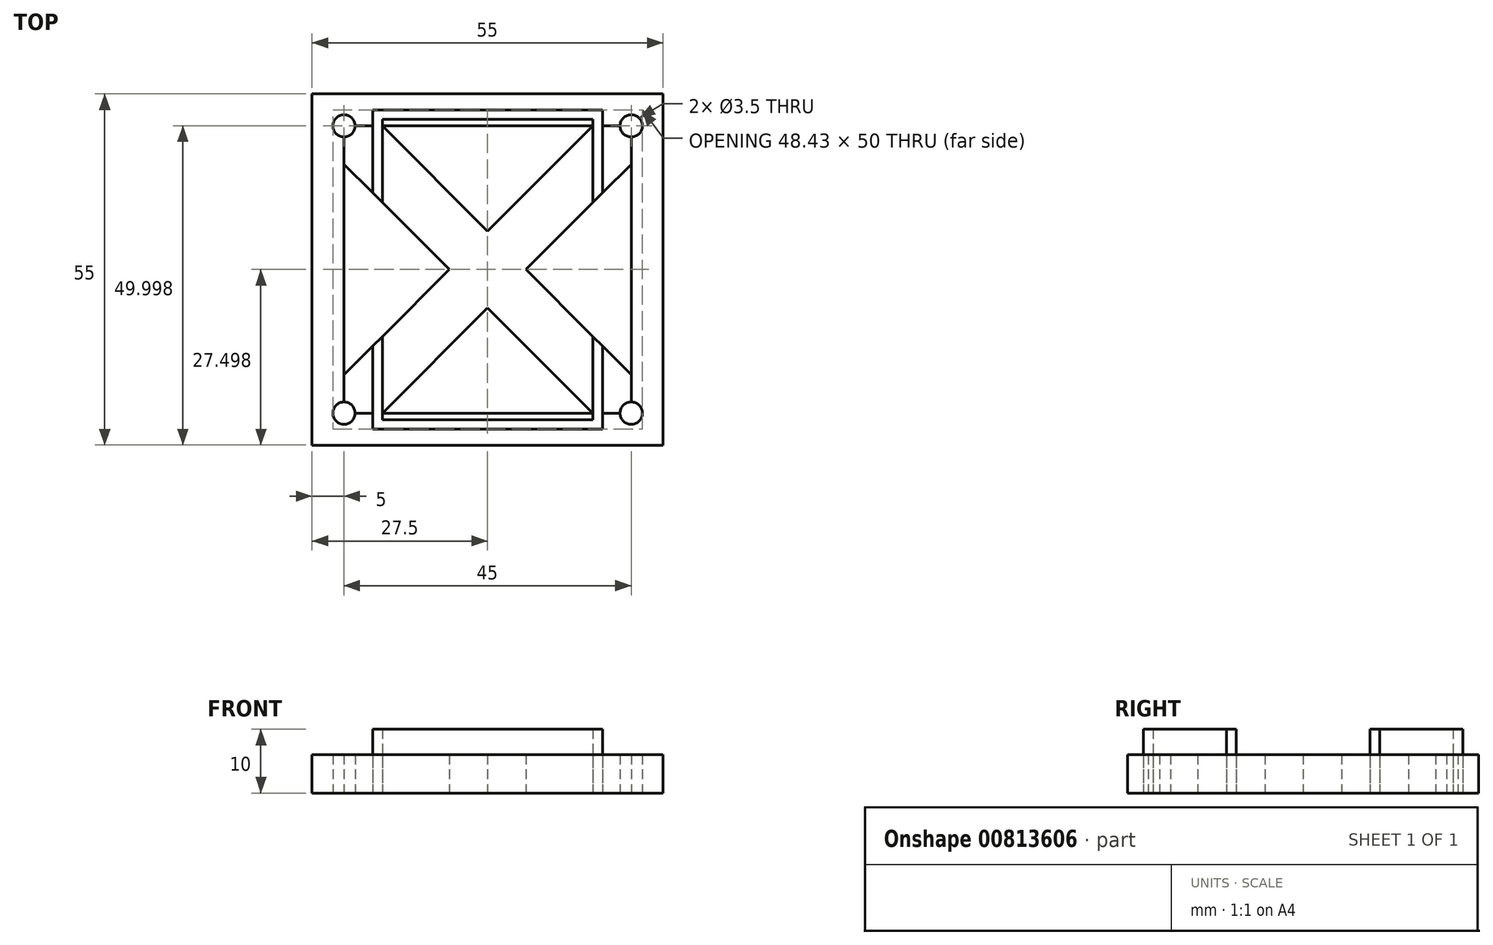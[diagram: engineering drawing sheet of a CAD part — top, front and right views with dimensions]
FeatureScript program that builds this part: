
annotation { "Feature Type Name" : "Feature", "Feature Type Description" : "" }
export const myFeature = defineFeature(function(context is Context, id is Id, definition is map)
    precondition{}
    {
        {
            var Q0;
            Q0=qCreatedBy(makeId("Top.planeOp"),FACE);
            var sketch = newSketch(context, id + "F0", { "sketchPlane" : qUnion([Q0])});
            skLineSegment(sketch, "E0.bottom", {"start": v(-44, 13.53) * mm, "end": v(11, 13.53) * mm});
            skLineSegment(sketch, "E0.top", {"start": v(-44, -41.47) * mm, "end": v(11, -41.47) * mm});
            skLineSegment(sketch, "E0.left", {"start": v(-44, 13.53) * mm, "end": v(-44, -41.47) * mm});
            skLineSegment(sketch, "E0.right", {"start": v(11, 13.53) * mm, "end": v(11, -41.47) * mm});
            skLineSegment(sketch, "E1.bottom", {"start": v(-39, 8.53) * mm, "end": v(6, 8.53) * mm});
            skLineSegment(sketch, "E1.top", {"start": v(-39, -36.47) * mm, "end": v(6, -36.47) * mm});
            skLineSegment(sketch, "E1.left", {"start": v(-39, 8.53) * mm, "end": v(-39, -36.47) * mm});
            skLineSegment(sketch, "E1.right", {"start": v(6, 8.53) * mm, "end": v(6, -36.47) * mm});
            skCircle(sketch, "E2", {"center": v(-39, 8.53) * mm, "radius": 1.75 * mm});
            skCircle(sketch, "E3", {"center": v(6, 8.53) * mm, "radius": 1.75 * mm});
            skCircle(sketch, "E4", {"center": v(6, -36.47) * mm, "radius": 1.75 * mm});
            skCircle(sketch, "E5", {"center": v(-39, -36.47) * mm, "radius": 1.75 * mm});
            skLineSegment(sketch, "E6.bottom", {"start": v(-33, 9.53) * mm, "end": v(0, 9.53) * mm});
            skLineSegment(sketch, "E6.top", {"start": v(-33, -37.47) * mm, "end": v(0, -37.47) * mm});
            skLineSegment(sketch, "E6.left", {"start": v(-33, 9.53) * mm, "end": v(-33, -37.47) * mm});
            skLineSegment(sketch, "E6.right", {"start": v(0, 9.53) * mm, "end": v(0, -37.47) * mm});
            skLineSegment(sketch, "E7.bottom", {"start": v(-34.5, 11.03) * mm, "end": v(1.5, 11.03) * mm});
            skLineSegment(sketch, "E7.top", {"start": v(-34.5, -38.97) * mm, "end": v(1.5, -38.97) * mm});
            skLineSegment(sketch, "E7.left", {"start": v(-34.5, 11.03) * mm, "end": v(-34.5, -38.97) * mm});
            skLineSegment(sketch, "E7.right", {"start": v(1.5, 11.03) * mm, "end": v(1.5, -38.97) * mm});
            skPoint(sketch, "E8", {"position": v(-16.38, -13.97) * mm});
            skPoint(sketch, "E9", {"position": v(-39, -30.47) * mm});
            skPoint(sketch, "E10", {"position": v(-33, -36.47) * mm});
            skPoint(sketch, "E11", {"position": v(0, -36.47) * mm});
            skPoint(sketch, "E12", {"position": v(6, -30.47) * mm});
            skPoint(sketch, "E13", {"position": v(6, 2.53) * mm});
            skPoint(sketch, "E14", {"position": v(0, 8.53) * mm});
            skPoint(sketch, "E15", {"position": v(-33, 8.53) * mm});
            skPoint(sketch, "E16", {"position": v(-39, 2.53) * mm});
            skLineSegment(sketch, "E17", {"start": v(-39, 2.53) * mm, "end": v(0, -36.47) * mm});
            skLineSegment(sketch, "E18", {"start": v(6, -30.47) * mm, "end": v(-33, 8.53) * mm});
            skLineSegment(sketch, "E19", {"start": v(0, 8.53) * mm, "end": v(-39, -30.47) * mm});
            skLineSegment(sketch, "E20", {"start": v(6, 2.53) * mm, "end": v(-33, -36.47) * mm});
            skSolve(sketch);
        }
        {
            var Q0;
            Q0=makeQuery(id+"F0.imprint","IMPRINT",FACE,{"disambiguationData":[TD([[makeQuery(id+"F0.imprint","IMPRINT",EDGE,{"derivedFrom":sQuery(id+"F0.wireOp",EDGE,"E0.bottom")}),-1.0]])]});
            var Q1;
            {var subQ0=sQuery(id+"F0.wireOp",EDGE,"E2");var subQ9=sQuery(id+"F0.wireOp",EDGE,"E1.bottom");var subQ10=makeQuery(id+"F0.imprint","INTERSECT",VERTEX,{"derivedFrom":[subQ9,subQ0]});Q1=makeQuery(id+"F0.imprint","IMPRINT",FACE,{"disambiguationData":[TD([[makeQuery(id+"F0.imprint","IMPRINT",EDGE,{"disambiguationData":[TD([[subQ10,-1.0]])],"derivedFrom":subQ9}),-1.0]])]});}
            var Q2;
            {var subQ5=sQuery(id+"F0.wireOp",EDGE,"E1.bottom");var subQ7=sQuery(id+"F0.wireOp",EDGE,"E7.right");var subQ11=makeQuery(id+"F0.imprint","INTERSECT",VERTEX,{"derivedFrom":[subQ5,subQ7]});Q2=makeQuery(id+"F0.imprint","IMPRINT",FACE,{"disambiguationData":[TD([[makeQuery(id+"F0.imprint","IMPRINT",EDGE,{"disambiguationData":[TD([[subQ11,-1.0]])],"derivedFrom":subQ5}),-1.0]])]});}
            var Q3;
            {var subQ5=sQuery(id+"F0.wireOp",EDGE,"E6.bottom");Q3=makeQuery(id+"F0.imprint","IMPRINT",FACE,{"disambiguationData":[TD([[makeQuery(id+"F0.imprint","IMPRINT",EDGE,{"derivedFrom":subQ5}),-1.0]])]});}
            var Q4;
            {var subQ5=sQuery(id+"F0.wireOp",EDGE,"E6.top");Q4=makeQuery(id+"F0.imprint","IMPRINT",FACE,{"disambiguationData":[TD([[makeQuery(id+"F0.imprint","IMPRINT",EDGE,{"derivedFrom":subQ5}),1.0]])]});}
            extrude(context, id + "F1", {"entities" : qUnion([Q0, Q1, Q2, Q3, Q4]), "depth" : 6 * mm, "offsetDistance" : 25 * mm});
        }
        {
            var Q0;
            {var subQ1=sQuery(id+"F0.wireOp",EDGE,"E6.bottom");Q0=makeQuery(id+"F0.imprint","IMPRINT",FACE,{"disambiguationData":[TD([[makeQuery(id+"F0.imprint","IMPRINT",EDGE,{"derivedFrom":subQ1}),1.0]])]});}
            var Q1;
            {var subQ0=sQuery(id+"F0.wireOp",EDGE,"E6.right");var subQ1=sQuery(id+"F0.wireOp",EDGE,"E1.bottom");var subQ2=makeQuery(id+"F0.imprint","INTERSECT",VERTEX,{"derivedFrom":[subQ1,subQ0]});Q1=makeQuery(id+"F0.imprint","IMPRINT",FACE,{"disambiguationData":[TD([[makeQuery(id+"F0.imprint","IMPRINT",EDGE,{"disambiguationData":[TD([[subQ2,-1.0]])],"derivedFrom":subQ1}),-1.0]])]});}
            var Q2;
            {var subQ0=sQuery(id+"F0.wireOp",EDGE,"E7.left");var subQ1=sQuery(id+"F0.wireOp",EDGE,"E1.bottom");var subQ2=makeQuery(id+"F0.imprint","INTERSECT",VERTEX,{"derivedFrom":[subQ1,subQ0]});Q2=makeQuery(id+"F0.imprint","IMPRINT",FACE,{"disambiguationData":[TD([[makeQuery(id+"F0.imprint","IMPRINT",EDGE,{"disambiguationData":[TD([[subQ2,-1.0]])],"derivedFrom":subQ1}),-1.0]])]});}
            var Q3;
            {var subQ1=sQuery(id+"F0.wireOp",EDGE,"E6.top");Q3=makeQuery(id+"F0.imprint","IMPRINT",FACE,{"disambiguationData":[TD([[makeQuery(id+"F0.imprint","IMPRINT",EDGE,{"derivedFrom":subQ1}),-1.0]])]});}
            var Q4;
            {var subQ1=sQuery(id+"F0.wireOp",EDGE,"E1.top");var subQ3=sQuery(id+"F0.wireOp",EDGE,"E7.left");var subQ4=makeQuery(id+"F0.imprint","INTERSECT",VERTEX,{"derivedFrom":[subQ1,subQ3]});Q4=makeQuery(id+"F0.imprint","IMPRINT",FACE,{"disambiguationData":[TD([[makeQuery(id+"F0.imprint","IMPRINT",EDGE,{"disambiguationData":[TD([[subQ4,1.0]])],"derivedFrom":subQ3}),1.0]])]});}
            var Q5;
            {var subQ1=sQuery(id+"F0.wireOp",EDGE,"E1.top");var subQ3=sQuery(id+"F0.wireOp",EDGE,"E7.right");var subQ4=makeQuery(id+"F0.imprint","INTERSECT",VERTEX,{"derivedFrom":[subQ1,subQ3]});Q5=makeQuery(id+"F0.imprint","IMPRINT",FACE,{"disambiguationData":[TD([[makeQuery(id+"F0.imprint","IMPRINT",EDGE,{"disambiguationData":[TD([[subQ4,1.0]])],"derivedFrom":subQ3}),-1.0]])]});}
            extrude(context, id + "F2", {"entities" : qUnion([Q0, Q1, Q2, Q3, Q4, Q5]), "depth" : 10 * mm, "offsetDistance" : 25 * mm});
        }
        {
            var Q0;
            {var subQ1=sQuery(id+"F0.wireOp",EDGE,"E6.left");var subQ3=sQuery(id+"F0.wireOp",EDGE,"E17");var subQ4=makeQuery(id+"F0.imprint","INTERSECT",VERTEX,{"derivedFrom":[subQ1,subQ3]});Q0=makeQuery(id+"F0.imprint","IMPRINT",FACE,{"disambiguationData":[TD([[makeQuery(id+"F0.imprint","IMPRINT",EDGE,{"disambiguationData":[TD([[subQ4,-1.0]])],"derivedFrom":subQ3}),1.0]])]});}
            var Q1;
            {var subQ1=sQuery(id+"F0.wireOp",EDGE,"E6.right");var subQ3=sQuery(id+"F0.wireOp",EDGE,"E18");var subQ4=makeQuery(id+"F0.imprint","INTERSECT",VERTEX,{"derivedFrom":[subQ1,subQ3]});Q1=makeQuery(id+"F0.imprint","IMPRINT",FACE,{"disambiguationData":[TD([[makeQuery(id+"F0.imprint","IMPRINT",EDGE,{"disambiguationData":[TD([[subQ4,-1.0]])],"derivedFrom":subQ3}),1.0]])]});}
            var Q2;
            {var subQ3=sQuery(id+"F0.wireOp",EDGE,"E19");var subQ5=sQuery(id+"F0.wireOp",EDGE,"E17");var subQ6=makeQuery(id+"F0.imprint","INTERSECT",VERTEX,{"derivedFrom":[subQ5,subQ3]});Q2=makeQuery(id+"F0.imprint","IMPRINT",FACE,{"disambiguationData":[TD([[makeQuery(id+"F0.imprint","IMPRINT",EDGE,{"disambiguationData":[TD([[subQ6,-1.0]])],"derivedFrom":subQ5}),-1.0]])]});}
            var Q3;
            {var subQ3=sQuery(id+"F0.wireOp",EDGE,"E20");var subQ5=sQuery(id+"F0.wireOp",EDGE,"E18");var subQ6=makeQuery(id+"F0.imprint","INTERSECT",VERTEX,{"derivedFrom":[subQ5,subQ3]});Q3=makeQuery(id+"F0.imprint","IMPRINT",FACE,{"disambiguationData":[TD([[makeQuery(id+"F0.imprint","IMPRINT",EDGE,{"disambiguationData":[TD([[subQ6,-1.0]])],"derivedFrom":subQ5}),-1.0]])]});}
            var Q4;
            {var subQ0=sQuery(id+"F0.wireOp",EDGE,"E7.right");var subQ1=sQuery(id+"F0.wireOp",EDGE,"E1.top");var subQ2=makeQuery(id+"F0.imprint","INTERSECT",VERTEX,{"derivedFrom":[subQ1,subQ0]});Q4=makeQuery(id+"F0.imprint","IMPRINT",FACE,{"disambiguationData":[TD([[makeQuery(id+"F0.imprint","IMPRINT",EDGE,{"disambiguationData":[TD([[subQ2,-1.0]])],"derivedFrom":subQ1}),1.0]])]});}
            var Q5;
            {var subQ0=sQuery(id+"F0.wireOp",EDGE,"E7.right");var subQ1=sQuery(id+"F0.wireOp",EDGE,"E1.bottom");var subQ2=makeQuery(id+"F0.imprint","INTERSECT",VERTEX,{"derivedFrom":[subQ1,subQ0]});Q5=makeQuery(id+"F0.imprint","IMPRINT",FACE,{"disambiguationData":[TD([[makeQuery(id+"F0.imprint","IMPRINT",EDGE,{"disambiguationData":[TD([[subQ2,-1.0]])],"derivedFrom":subQ1}),-1.0]])]});}
            var Q6;
            {var subQ1=sQuery(id+"F0.wireOp",EDGE,"E1.bottom");var subQ5=sQuery(id+"F0.wireOp",EDGE,"E2");var subQ6=makeQuery(id+"F0.imprint","INTERSECT",VERTEX,{"derivedFrom":[subQ1,subQ5]});Q6=makeQuery(id+"F0.imprint","IMPRINT",FACE,{"disambiguationData":[TD([[makeQuery(id+"F0.imprint","IMPRINT",EDGE,{"disambiguationData":[TD([[subQ6,-1.0]])],"derivedFrom":subQ1}),-1.0]])]});}
            var Q7;
            {var subQ1=sQuery(id+"F0.wireOp",EDGE,"E1.top");var subQ5=sQuery(id+"F0.wireOp",EDGE,"E5");var subQ6=makeQuery(id+"F0.imprint","INTERSECT",VERTEX,{"derivedFrom":[subQ1,subQ5]});Q7=makeQuery(id+"F0.imprint","IMPRINT",FACE,{"disambiguationData":[TD([[makeQuery(id+"F0.imprint","IMPRINT",EDGE,{"disambiguationData":[TD([[subQ6,-1.0]])],"derivedFrom":subQ1}),1.0]])]});}
            var Q8;
            {var subQ0=sQuery(id+"F0.wireOp",EDGE,"E19");var subQ1=sQuery(id+"F0.wireOp",EDGE,"E17");var subQ2=makeQuery(id+"F0.imprint","INTERSECT",VERTEX,{"derivedFrom":[subQ1,subQ0]});Q8=makeQuery(id+"F0.imprint","IMPRINT",FACE,{"disambiguationData":[TD([[makeQuery(id+"F0.imprint","IMPRINT",EDGE,{"disambiguationData":[TD([[subQ2,-1.0]])],"derivedFrom":subQ1}),1.0]])]});}
            extrude(context, id + "F3", {"entities" : qUnion([Q0, Q1, Q2, Q3, Q4, Q5, Q6, Q7, Q8]), "depth" : 6 * mm, "offsetDistance" : 25 * mm});
        }
    });
